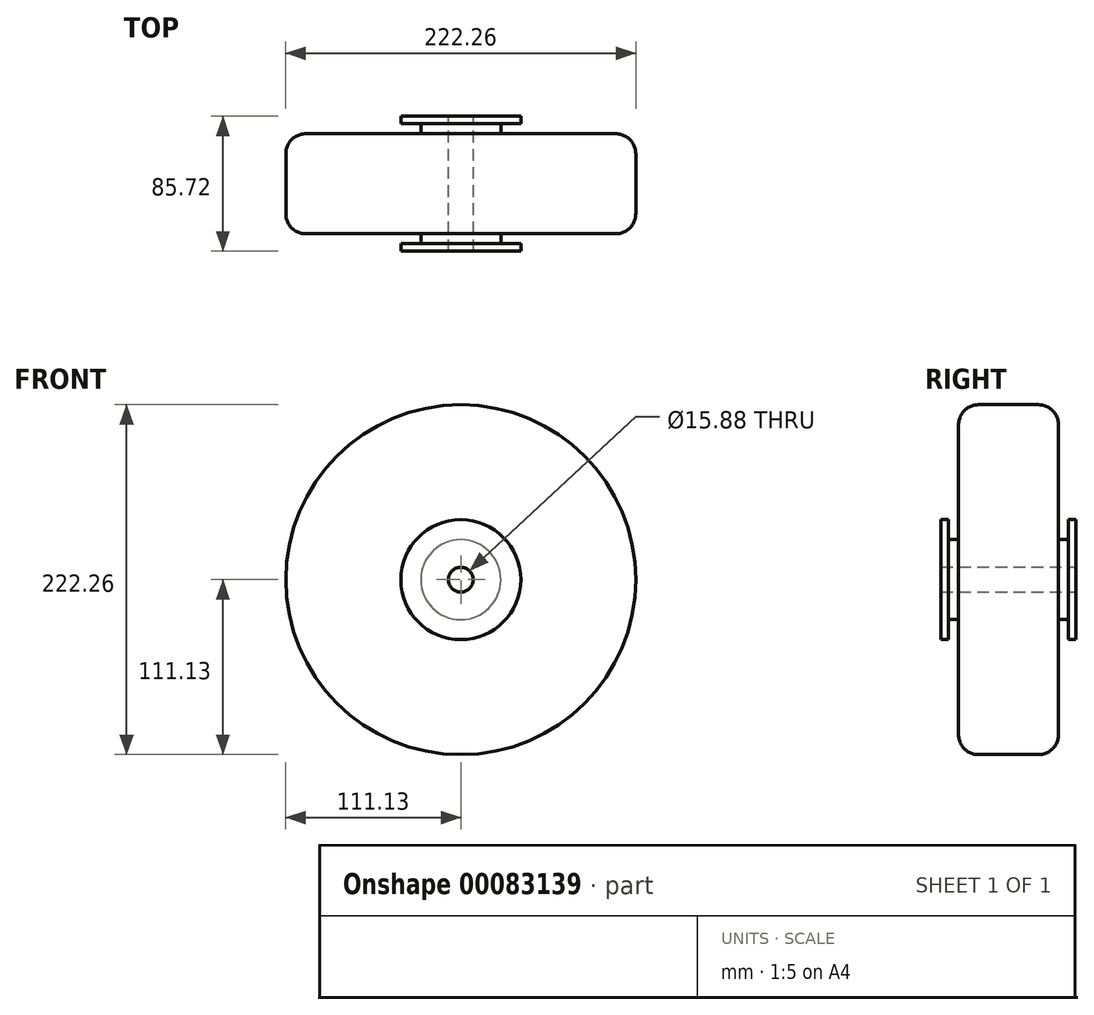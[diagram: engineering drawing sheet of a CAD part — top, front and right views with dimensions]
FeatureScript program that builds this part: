
annotation { "Feature Type Name" : "Feature", "Feature Type Description" : "" }
export const myFeature = defineFeature(function(context is Context, id is Id, definition is map)
    precondition{}
    {
        {
            var Q0;
            Q0=qCreatedBy(makeId("Front.planeOp"),FACE);
            var sketch = newSketch(context, id + "F0", { "sketchPlane" : qUnion([Q0])});
            skCircle(sketch, "E0", {"center": v(0, 0) * mm, "radius": 111.13 * mm});
            skCircle(sketch, "E1", {"center": v(0, 0) * mm, "radius": 7.94 * mm});
            skSolve(sketch);
        }
        {
            var Q0;
            Q0=makeQuery(id+"F0.imprint","IMPRINT",FACE,{"disambiguationData":[TD([[makeQuery(id+"F0.imprint","IMPRINT",EDGE,{"derivedFrom":sQuery(id+"F0.wireOp",EDGE,"E0")}),1.0]])]});
            extrude(context, id + "F1", {"entities" : qUnion([Q0]), "depth" : 63.5 * mm});
        }
        {
            var Q0;
            Q0=makeQuery(id+"F1.opExtrude","CAP_EDGE",EDGE,{"disambiguationData":[OSD([sQuery(id+"F0.wireOp",EDGE,"E0")])],"isStart":false});
            fillet(context, id + "F2", {"entities" : qUnion([Q0]), "radius" : 12.7 * mm, "tangentPropagation" : true, "allowEdgeOverflow" : false});
        }
        {
            var Q0;
            Q0=makeQuery(id+"F1.opExtrude","CAP_EDGE",EDGE,{"disambiguationData":[OSD([sQuery(id+"F0.wireOp",EDGE,"E0")])],"isStart":true});
            fillet(context, id + "F3", {"entities" : qUnion([Q0]), "radius" : 12.7 * mm, "tangentPropagation" : true, "allowEdgeOverflow" : false});
        }
        {
            var Q0;
            Q0=makeQuery(id+"F1.opExtrude","CAP_FACE",FACE,{"disambiguationData":[OSD([sQuery(id+"F0.wireOp",EDGE,"E0"),sQuery(id+"F0.wireOp",EDGE,"E1")])],"isStart":false});
            var sketch = newSketch(context, id + "F4", { "sketchPlane" : qUnion([Q0])});
            skCircle(sketch, "E2", {"center": v(0, 0) * mm, "radius": 25.4 * mm});
            skSolve(sketch);
        }
        {
            var Q0;
            Q0=makeQuery(id+"F4.imprint","IMPRINT",FACE,{"disambiguationData":[TD([[makeQuery(id+"F4.imprint","IMPRINT",EDGE,{"derivedFrom":sQuery(id+"F4.wireOp",EDGE,"E2")}),1.0]])]});
            extrude(context, id + "F5", {"entities" : qUnion([Q0]), "operationType" : NewBodyOperationType.ADD, "depth" : 6.35 * mm});
        }
        {
            var Q0;
            Q0=makeQuery(id+"F5.opExtrude","CAP_FACE",FACE,{"disambiguationData":[OSD([sQuery(id+"F0.wireOp",EDGE,"E1"),sQuery(id+"F4.wireOp",EDGE,"E2")])],"isStart":false});
            var sketch = newSketch(context, id + "F6", { "sketchPlane" : qUnion([Q0])});
            skCircle(sketch, "E3", {"center": v(0, 0) * mm, "radius": 38.1 * mm});
            skSolve(sketch);
        }
        {
            var Q0;
            Q0=makeQuery(id+"F6.imprint","IMPRINT",FACE,{"disambiguationData":[TD([[makeQuery(id+"F6.imprint","IMPRINT",EDGE,{"derivedFrom":sQuery(id+"F6.wireOp",EDGE,"E3")}),1.0]])]});
            extrude(context, id + "F7", {"entities" : qUnion([Q0]), "depth" : 4.76 * mm});
        }
        {
            var Q0;
            Q0=makeQuery(id+"F1.opExtrude","CAP_FACE",FACE,{"disambiguationData":[OSD([sQuery(id+"F0.wireOp",EDGE,"E0"),sQuery(id+"F0.wireOp",EDGE,"E1")])],"isStart":true});
            var sketch = newSketch(context, id + "F8", { "sketchPlane" : qUnion([Q0])});
            skCircle(sketch, "E4", {"center": v(0, 0) * mm, "radius": 25.4 * mm});
            skSolve(sketch);
        }
        {
            var Q0;
            Q0=makeQuery(id+"F8.imprint","IMPRINT",FACE,{"disambiguationData":[TD([[makeQuery(id+"F8.imprint","IMPRINT",EDGE,{"derivedFrom":sQuery(id+"F8.wireOp",EDGE,"E4")}),1.0]])]});
            extrude(context, id + "F9", {"entities" : qUnion([Q0]), "operationType" : NewBodyOperationType.ADD, "depth" : 6.35 * mm});
        }
        {
            var Q0;
            Q0=makeQuery(id+"F9.opExtrude","CAP_FACE",FACE,{"disambiguationData":[OSD([sQuery(id+"F0.wireOp",EDGE,"E1"),sQuery(id+"F8.wireOp",EDGE,"E4")])],"isStart":false});
            var sketch = newSketch(context, id + "F10", { "sketchPlane" : qUnion([Q0])});
            skCircle(sketch, "E5", {"center": v(0, 0) * mm, "radius": 38.1 * mm});
            skSolve(sketch);
        }
        {
            var Q0;
            Q0=makeQuery(id+"F10.imprint","IMPRINT",FACE,{"disambiguationData":[TD([[makeQuery(id+"F10.imprint","IMPRINT",EDGE,{"derivedFrom":sQuery(id+"F10.wireOp",EDGE,"E5")}),1.0]])]});
            extrude(context, id + "F11", {"entities" : qUnion([Q0]), "depth" : 4.76 * mm});
        }
        {
            var Q0;
            Q0=makeQuery(id+"F11.opExtrude","SWEPT_BODY",BODY,{"disambiguationData":[OSD([sQuery(id+"F8.wireOp",EDGE,"E4"),sQuery(id+"F10.wireOp",EDGE,"E5")])]});
            deleteBodies(context, id + "F12", {"entities" : qUnion([Q0])});
        }
        {
            var Q0;
            Q0=makeQuery(id+"F7.opExtrude","SWEPT_BODY",BODY,{"disambiguationData":[OSD([sQuery(id+"F4.wireOp",EDGE,"E2"),sQuery(id+"F6.wireOp",EDGE,"E3")])]});
            deleteBodies(context, id + "F13", {"entities" : qUnion([Q0])});
        }
        {
            var Q0;
            Q0=makeQuery(id+"F5.opExtrude","CAP_FACE",FACE,{"disambiguationData":[OSD([sQuery(id+"F0.wireOp",EDGE,"E1"),sQuery(id+"F4.wireOp",EDGE,"E2")])],"isStart":false});
            var sketch = newSketch(context, id + "F14", { "sketchPlane" : qUnion([Q0])});
            skCircle(sketch, "E6", {"center": v(0, 0) * mm, "radius": 38.1 * mm});
            skSolve(sketch);
        }
        {
            var Q0;
            Q0=makeQuery(id+"F14.imprint","IMPRINT",FACE,{"disambiguationData":[TD([[makeQuery(id+"F14.imprint","IMPRINT",EDGE,{"derivedFrom":makeQuery(id+"F5.opExtrude","CAP_EDGE",EDGE,{"disambiguationData":[OSD([sQuery(id+"F4.wireOp",EDGE,"E2")])],"isStart":false})}),1.0]])]});
            var Q1;
            Q1=makeQuery(id+"F14.imprint","IMPRINT",FACE,{"disambiguationData":[TD([[makeQuery(id+"F14.imprint","IMPRINT",EDGE,{"derivedFrom":sQuery(id+"F14.wireOp",EDGE,"E6")}),1.0]])]});
            extrude(context, id + "F15", {"entities" : qUnion([Q0, Q1]), "operationType" : NewBodyOperationType.ADD, "depth" : 4.76 * mm});
        }
        {
            var Q0;
            Q0=makeQuery(id+"F9.opExtrude","CAP_FACE",FACE,{"disambiguationData":[OSD([sQuery(id+"F0.wireOp",EDGE,"E1"),sQuery(id+"F8.wireOp",EDGE,"E4")])],"isStart":false});
            var sketch = newSketch(context, id + "F16", { "sketchPlane" : qUnion([Q0])});
            skCircle(sketch, "E7", {"center": v(0, 0) * mm, "radius": 38.1 * mm});
            skSolve(sketch);
        }
        {
            var Q0;
            Q0=makeQuery(id+"F16.imprint","IMPRINT",FACE,{"disambiguationData":[TD([[makeQuery(id+"F16.imprint","IMPRINT",EDGE,{"derivedFrom":makeQuery(id+"F9.opExtrude","CAP_EDGE",EDGE,{"disambiguationData":[OSD([sQuery(id+"F8.wireOp",EDGE,"E4")])],"isStart":false})}),1.0]])]});
            var Q1;
            Q1=makeQuery(id+"F16.imprint","IMPRINT",FACE,{"disambiguationData":[TD([[makeQuery(id+"F16.imprint","IMPRINT",EDGE,{"derivedFrom":sQuery(id+"F16.wireOp",EDGE,"E7")}),1.0]])]});
            extrude(context, id + "F17", {"entities" : qUnion([Q0, Q1]), "operationType" : NewBodyOperationType.ADD, "depth" : 4.76 * mm});
        }
    });
